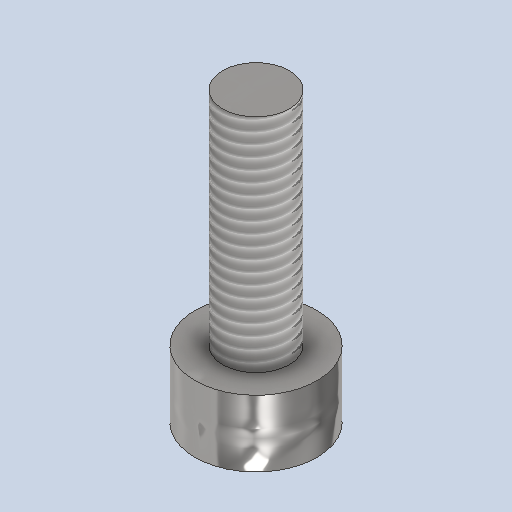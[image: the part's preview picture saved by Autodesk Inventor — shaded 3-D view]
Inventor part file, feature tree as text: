
AUTODESK INVENTOR PART (.ipt)
format: ipt  version: 2024.2 (Build 282272000, 272)  size: 175,104 bytes
history: native  units: mm
features: sketch x2, revolve x1, thread x1, extrude x1
ambient origin geometry x8: Origin, YZ Plane, XZ Plane, XY Plane, X Axis, Y Axis, Z Axis, Center Point
bodies: Solid1 (feature_tree)
feature tree (5):
  revolve  "Revolution1"  [1 undecoded]
  thread  "Thread1"  [1 undecoded]
  extrude  "Extrusion1"  [1 undecoded]
  sketch  "Sketch1"  dims[d4=90.0deg d5=6.0mm d6=0.0mm d0=0.0mm]
  sketch  "Sketch2"
note: 3 required parameter values undecoded (feature->parameter linkage not recoverable at this tier; creation-order binding heuristic only, values carry confidence <= 0.55)